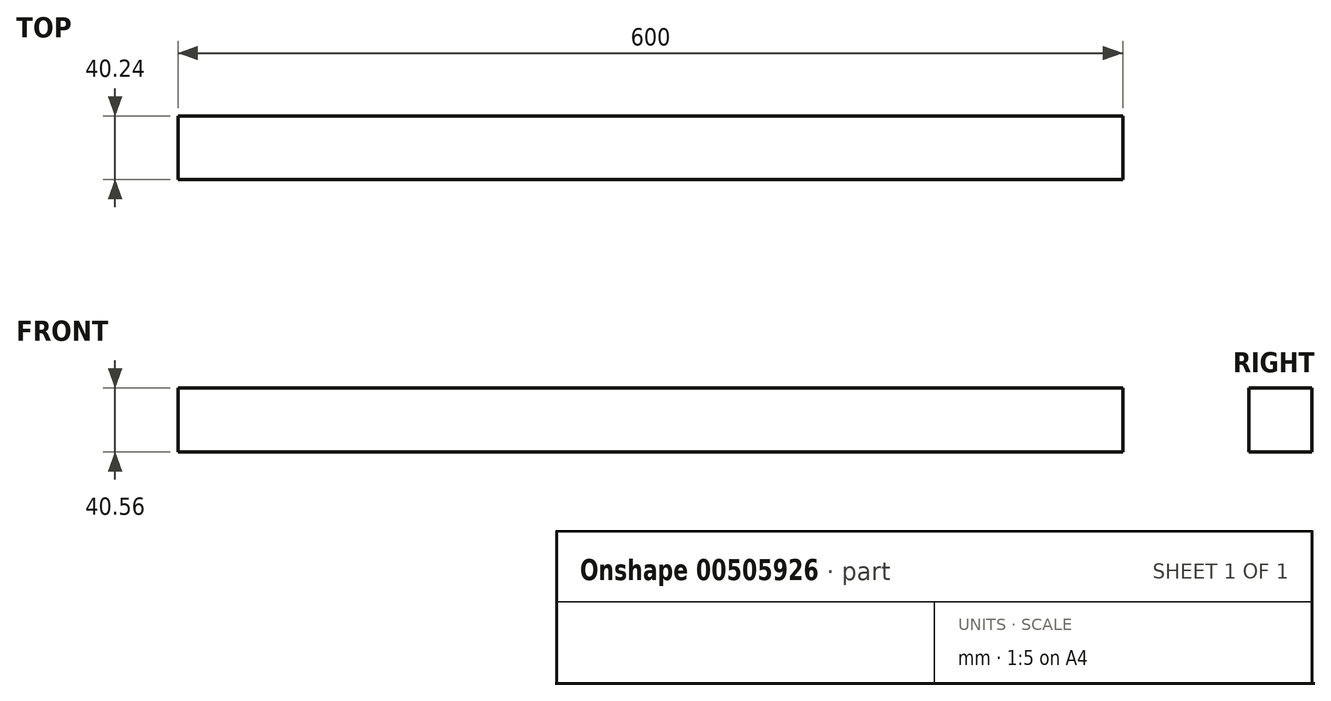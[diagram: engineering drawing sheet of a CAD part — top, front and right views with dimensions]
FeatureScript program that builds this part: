
annotation { "Feature Type Name" : "Feature", "Feature Type Description" : "" }
export const myFeature = defineFeature(function(context is Context, id is Id, definition is map)
    precondition{}
    {
        {
            var Q0;
            Q0=qCreatedBy(makeId("Right.planeOp"),FACE);
            var sketch = newSketch(context, id + "F0", { "sketchPlane" : qUnion([Q0])});
            skLineSegment(sketch, "E0.bottom", {"start": v(0, 0) * mm, "end": v(-40.24, 0) * mm});
            skLineSegment(sketch, "E0.top", {"start": v(0, 40.56) * mm, "end": v(-40.24, 40.56) * mm});
            skLineSegment(sketch, "E0.left", {"start": v(0, 0) * mm, "end": v(0, 40.56) * mm});
            skLineSegment(sketch, "E0.right", {"start": v(-40.24, 0) * mm, "end": v(-40.24, 40.56) * mm});
            skSolve(sketch);
        }
        {
            var Q0;
            Q0=makeQuery(id+"F0.imprint","IMPRINT",FACE,{"disambiguationData":[TD([[makeQuery(id+"F0.imprint","IMPRINT",EDGE,{"derivedFrom":sQuery(id+"F0.wireOp",EDGE,"E0.bottom")}),-1.0]])]});
            extrude(context, id + "F1", {"entities" : qUnion([Q0]), "depth" : 600 * mm});
        }
    });
